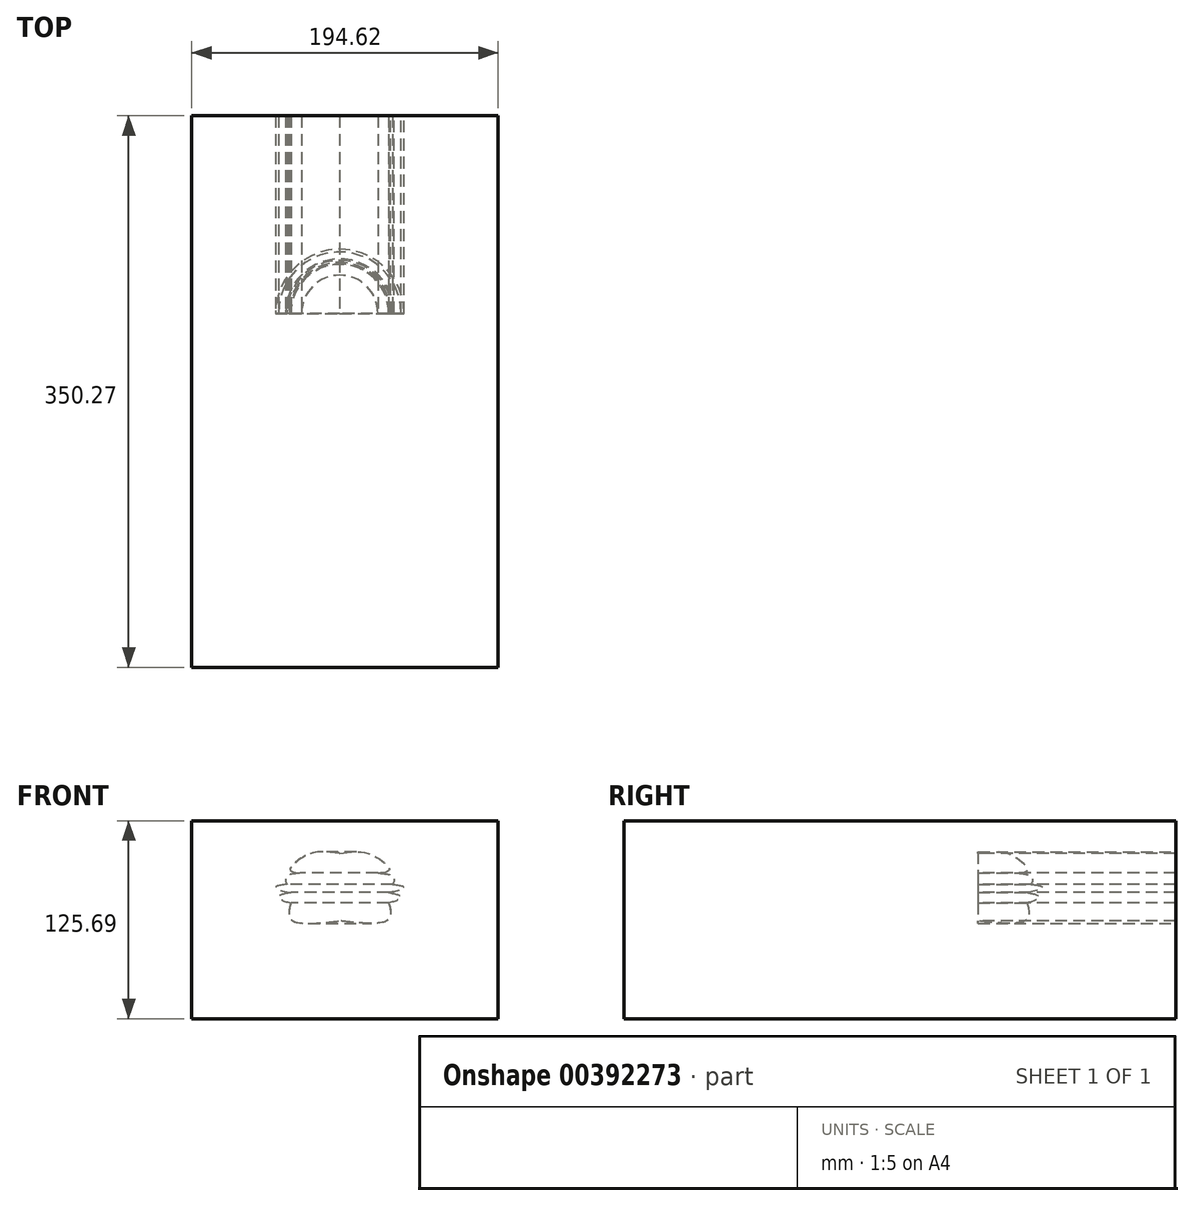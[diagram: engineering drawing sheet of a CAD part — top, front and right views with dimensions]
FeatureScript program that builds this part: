
annotation { "Feature Type Name" : "Feature", "Feature Type Description" : "" }
export const myFeature = defineFeature(function(context is Context, id is Id, definition is map)
    precondition{}
    {
        {
            var Q0;
            Q0=qCreatedBy(makeId("Front.planeOp"),FACE);
            var sketch = newSketch(context, id + "F0", { "sketchPlane" : qUnion([Q0])});
            skFitSpline(sketch, "E0", {"points": [v(0, 56.24) * mm, v(0, -46.18) * mm], "startDerivative": vector(0, -102.41) * mm, "endDerivative": vector(0, -102.41) * mm});
            skFitSpline(sketch, "E1", {"points": [v(0, 56.24) * mm, v(17.68, 56.24) * mm, v(29.26, 49.23) * mm, v(31.4, 45.26) * mm, v(0, 44.65) * mm], "startDerivative": vector(68.58, 8.28) * mm, "endDerivative": vector(-123.73, 7.98) * mm});
            skFitSpline(sketch, "E2", {"points": [v(24.25, 43.7) * mm, v(34.44, 40.39) * mm, v(31.09, 34.6) * mm, v(20.12, 37.95) * mm, v(9.75, 33.99) * mm, v(3.96, 37.95) * mm, v(0, 40.39) * mm], "startDerivative": vector(74.39, -6.45) * mm, "endDerivative": vector(-31.29, 14.58) * mm});
            skFitSpline(sketch, "E3", {"points": [v(33.64, 36.54) * mm, v(40.84, 34.6) * mm, v(31.09, 31.24) * mm, v(14.8, 31.85) * mm, v(0, 31.24) * mm], "startDerivative": vector(54.89, -7.64) * mm, "endDerivative": vector(-53.08, -4.7) * mm});
            skFitSpline(sketch, "E4", {"points": [v(31.09, 31.24) * mm, v(39.01, 28.5) * mm, v(31.09, 24.84) * mm, v(14.8, 25.76) * mm, v(0, 22.1) * mm], "startDerivative": vector(56.21, -10.56) * mm, "endDerivative": vector(-51.43, -18.92) * mm});
            skFitSpline(sketch, "E5", {"points": [v(31.09, 24.84) * mm, v(31.09, 14.17) * mm, v(0, 13.26) * mm], "startDerivative": vector(9.1, -33.95) * mm, "endDerivative": vector(-64.84, 7.2) * mm});
            skLineSegment(sketch, "E6", {"start": v(0, 56.24) * mm, "end": v(0, 13.26) * mm});
            skSolve(sketch);
        }
        {
            var Q0;
            {var subQ0=sQuery(id+"F0.wireOp",EDGE,"E6");var subQ1=sQuery(id+"F0.wireOp",EDGE,"E1");var subQ2=makeQuery(id+"F0.imprint","INTERSECT",VERTEX,{"disambiguationData":[OD(0.0)],"derivedFrom":[subQ1,subQ0]});Q0=makeQuery(id+"F0.imprint","IMPRINT",FACE,{"disambiguationData":[TD([[makeQuery(id+"F0.imprint","IMPRINT",EDGE,{"disambiguationData":[TD([[subQ2,-1.0]])],"derivedFrom":subQ1}),-1.0]])]});}
            var Q1;
            {var subQ0=sQuery(id+"F0.wireOp",EDGE,"E6");var subQ1=sQuery(id+"F0.wireOp",EDGE,"E1");var subQ2=makeQuery(id+"F0.imprint","INTERSECT",VERTEX,{"disambiguationData":[OD(1.0)],"derivedFrom":[subQ1,subQ0]});Q1=makeQuery(id+"F0.imprint","IMPRINT",FACE,{"disambiguationData":[TD([[makeQuery(id+"F0.imprint","IMPRINT",EDGE,{"disambiguationData":[TD([[subQ2,1.0]])],"derivedFrom":subQ1}),1.0]])]});}
            var Q2;
            {var subQ0=sQuery(id+"F0.wireOp",EDGE,"E6");var subQ1=sQuery(id+"F0.wireOp",EDGE,"E2");var subQ2=makeQuery(id+"F0.imprint","INTERSECT",VERTEX,{"derivedFrom":[subQ1,subQ0]});Q2=makeQuery(id+"F0.imprint","IMPRINT",FACE,{"disambiguationData":[TD([[makeQuery(id+"F0.imprint","IMPRINT",EDGE,{"disambiguationData":[TD([[subQ2,1.0]])],"derivedFrom":subQ1}),1.0]])]});}
            var Q3;
            {var subQ0=sQuery(id+"F0.wireOp",EDGE,"E6");var subQ1=sQuery(id+"F0.wireOp",EDGE,"E3");var subQ2=makeQuery(id+"F0.imprint","INTERSECT",VERTEX,{"derivedFrom":[subQ1,subQ0]});Q3=makeQuery(id+"F0.imprint","IMPRINT",FACE,{"disambiguationData":[TD([[makeQuery(id+"F0.imprint","IMPRINT",EDGE,{"disambiguationData":[TD([[subQ2,1.0]])],"derivedFrom":subQ1}),1.0]])]});}
            var Q4;
            {var subQ3=sQuery(id+"F0.wireOp",EDGE,"E5");Q4=makeQuery(id+"F0.imprint","IMPRINT",FACE,{"disambiguationData":[TD([[makeQuery(id+"F0.imprint","IMPRINT",EDGE,{"derivedFrom":subQ3}),-1.0]])]});}
            var Q5;
            Q5=sQuery(id+"F0.wireOp",EDGE,"E6");
            revolve(context, id + "F1", {"entities" : qUnion([Q0, Q1, Q2, Q3, Q4]), "axis" : qUnion([Q5]), "revolveType" : RevolveType.FULL});
        }
        {
            var Q0;
            Q0=qCreatedBy(makeId("Front.planeOp"),FACE);
            var sketch = newSketch(context, id + "F2", { "sketchPlane" : qUnion([Q0])});
            skLineSegment(sketch, "E7.bottom", {"start": v(-94, 76.84) * mm, "end": v(100.6, 76.84) * mm});
            skLineSegment(sketch, "E7.top", {"start": v(-94, -48.85) * mm, "end": v(100.6, -48.85) * mm});
            skLineSegment(sketch, "E7.left", {"start": v(-94, 76.84) * mm, "end": v(-94, -48.85) * mm});
            skLineSegment(sketch, "E7.right", {"start": v(100.6, 76.84) * mm, "end": v(100.6, -48.85) * mm});
            skSolve(sketch);
        }
        {
            var Q0;
            Q0=makeQuery(id+"F2.imprint","IMPRINT",FACE,{"disambiguationData":[TD([[makeQuery(id+"F2.imprint","IMPRINT",EDGE,{"derivedFrom":sQuery(id+"F2.wireOp",EDGE,"E7.bottom")}),-1.0]])]});
            extrude(context, id + "F3", {"entities" : qUnion([Q0]), "operationType" : NewBodyOperationType.ADD, "depth" : 224.79 * mm});
        }
        {
            var Q0;
            Q0=makeQuery(id+"F3.opExtrude","CAP_FACE",FACE,{"disambiguationData":[OSD([sQuery(id+"F2.wireOp",EDGE,"E7.bottom"),sQuery(id+"F2.wireOp",EDGE,"E7.top"),sQuery(id+"F2.wireOp",EDGE,"E7.left"),sQuery(id+"F2.wireOp",EDGE,"E7.right")])],"isStart":true});
            extrude(context, id + "F4", {"entities" : qUnion([Q0]), "operationType" : NewBodyOperationType.ADD, "depth" : 125.48 * mm});
        }
    });
